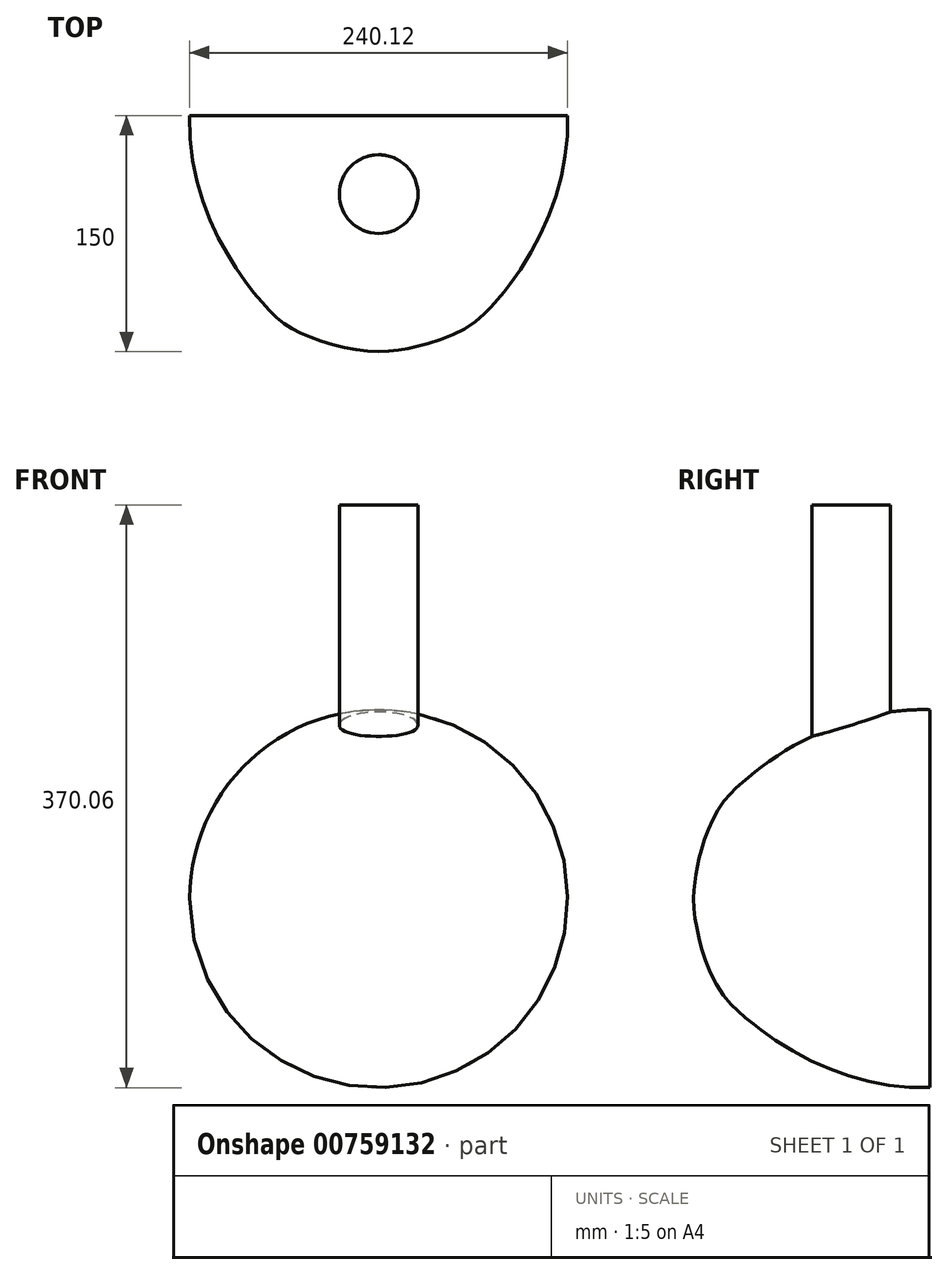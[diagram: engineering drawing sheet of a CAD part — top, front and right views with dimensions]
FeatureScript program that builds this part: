
annotation { "Feature Type Name" : "Feature", "Feature Type Description" : "" }
export const myFeature = defineFeature(function(context is Context, id is Id, definition is map)
    precondition{}
    {
        {
            var Q0;
            Q0=qCreatedBy(makeId("Top.planeOp"),FACE);
            var sketch = newSketch(context, id + "F0", { "sketchPlane" : qUnion([Q0])});
            skLineSegment(sketch, "E0", {"start": v(0, 0) * mm, "end": v(0, 150) * mm});
            skLineSegment(sketch, "E1", {"start": v(0, 150) * mm, "end": v(-120, 150) * mm});
            skFitSpline(sketch, "E2", {"points": [v(-120, 150) * mm, v(-76.2, 33.72) * mm, v(-47.32, 10.78) * mm, v(0, 0) * mm], "startDerivative": vector(-9.6, -344.99) * mm, "endDerivative": vector(152.96, 0) * mm});
            skSolve(sketch);
        }
        {
            var Q0;
            Q0 = qSketchRegion(id + "F0", true);
            var Q1;
            Q1=sQuery(id+"F0.wireOp",EDGE,"E0");
            revolve(context, id + "F1", {"surfaceOperationType" : NewSurfaceOperationType.NEW, "entities" : qUnion([Q0]), "axis" : qUnion([Q1]), "revolveType" : RevolveType.FULL});
        }
        {
            var Q0;
            Q0=qCreatedBy(makeId("Top.planeOp"),FACE);
            var sketch = newSketch(context, id + "F2", { "sketchPlane" : qUnion([Q0])});
            skLineSegment(sketch, "E3", {"start": v(0, 0) * mm, "end": v(0, 100) * mm});
            skCircle(sketch, "E4", {"center": v(0, 100) * mm, "radius": 25 * mm});
            skSolve(sketch);
        }
        {
            var Q0;
            Q0 = qSketchRegion(id + "F2", true);
            extrude(context, id + "F3", {"entities" : qUnion([Q0]), "operationType" : NewBodyOperationType.ADD, "depth" : 250 * mm, "offsetDistance" : 25 * mm});
        }
    });
